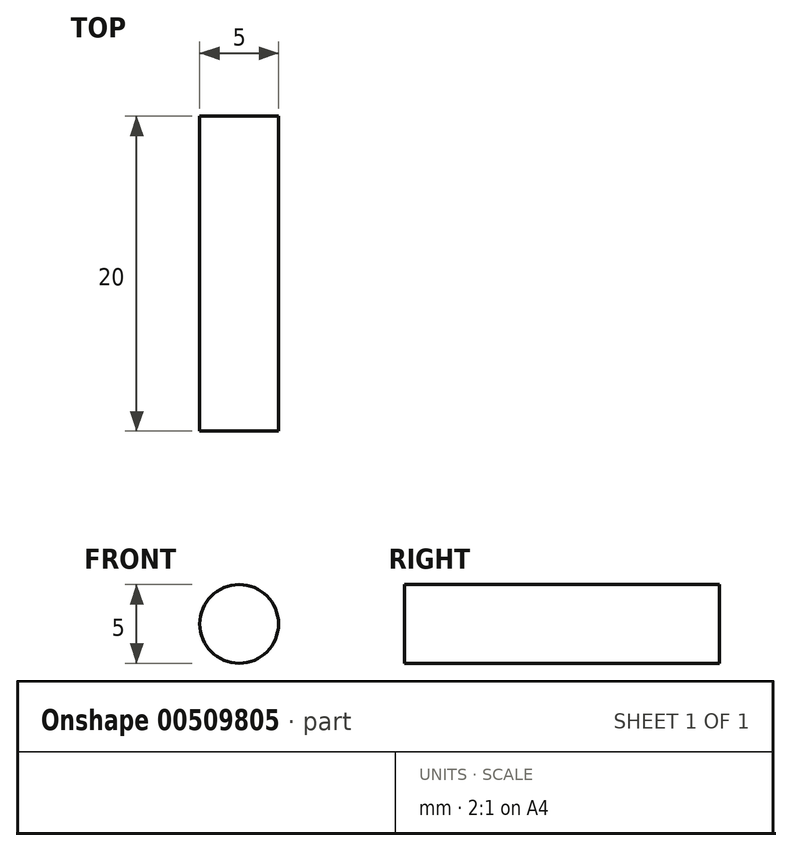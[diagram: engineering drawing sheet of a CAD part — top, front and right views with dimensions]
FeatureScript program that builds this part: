
annotation { "Feature Type Name" : "Feature", "Feature Type Description" : "" }
export const myFeature = defineFeature(function(context is Context, id is Id, definition is map)
    precondition{}
    {
        {
            var Q0;
            Q0=qCreatedBy(makeId("Front.planeOp"),FACE);
            var sketch = newSketch(context, id + "F0", { "sketchPlane" : qUnion([Q0])});
            skCircle(sketch, "E0", {"center": v(0, 0) * mm, "radius": 2.5 * mm});
            skSolve(sketch);
        }
        {
            var Q0;
            Q0=sQuery(id+"F0.wireOp",EDGE,"E0");
            extrude(context, id + "F1", {"bodyType" : ToolBodyType.SURFACE, "surfaceEntities" : qUnion([Q0]), "depth" : 20 * mm, "offsetDistance" : 25 * mm});
        }
    });
